# Revit family: Lighting-SIMES-S.5570W-MEGAZIP_DOWNLIGHT_ROUND
name_source: partatom
category: Lighting Fixtures
revit_build: Autodesk Revit 2016 (Build: 20150701_1515(x64)
units: mm (PartAtom-declared; Revit-internal decimal feet)

## family parameters
Cut with Voids When Loaded = No
Host = Face
Light Source = Yes
OmniClass Number = 23.80.70.14
OmniClass Title = Luminaries for External Lighting
Part Type = Normal
Room Calculation Point = No
Round Connector Dimension = Use Diameter
Shared = No

## types (1)
- Lighting-SIMES-S.5570W-MEGAZIP_DOWNLIGHT_ROUND
    Approval mark = CE
    BIMobject category = Outside
    Brand url = http://www.simes.it
    Color Filter = 16777215
    Color Rendering Index = CRI 90
    Colour Temperature = 3000
    Control Gear = magnetic transformer
    Date of publishing = 11/5/2015
    Default Elevation = 1219 mm
    Description = MEGAZIP DOWNLIGHT ROUND
Art. S.5570W.19
MODULES LED 3000K  230V 24.3W CRI 90
Rated luminaire luminous flux: 1280lm
Rated input power: 27W
Luminaire efficacy: 47lm/W
Electronic ballast 220÷240V 0/50/60Hz
CE

Fixture available with integral DALI driver on request with surcharge.

PRODUCT TYPE
False ceiling-recessed down-light fitting. Recessing depth 216 mm. IP rating IP 65
MATERIAL CHARACTERISTICS
"Copper Free" Aluminium die cast housing in EN AB-44100 with high resistance against corrosion. Stone wash surface treatment prior to painting process. 2 mm thick front trim in  Stainless Steel - Grade AISI 316L with 2,5-3% molybdenum content. A4 grade Stainless Steel screws with 2,5-3% molybdenum content which increases the resistance against corrosion. Pre treated Silicone Gaskets. Painting Process : 3 Step Process
1) Surface treatment with BONDERITE. A heavy metal free chemical surface treatment containing ceramic nano particles giving a cohesive, inorganic and highly dense protective coating. 2) PRE POLYMERIZATION a process of introducing an epoxy primer with excellent characteristics to the paint which also offers very high resistance to oxidation due to its Zinc content. 3) POLYMERIZATION a process with the application of polyester powder with high resistance against UV rays and harsh weather conditions. Resistance test protection for Marine applications for 1500h.  Mechanical resistance of diffuser IK 09
LIGHTING PERFORMANCE
Reflector in 99.98% pure anodized aluminium . Toughened  semiacid-etched  glass 12mm thick. Lamp  adjustable ±15° position. LOR -- 
INSTALLATION AND MANTEINANCE
The luminaires are fixed to the falseceiling by a heavy-duty bracket system, adjustable from inside the luminaire. Model comes with a steel safety wire. Front re-lamping without removing the complete fitting from the ceiling.
WIRING
Double cable entry with cable glands PG 13.5 (Ø 6÷12 mm) . Isolation: CLASS I . Available colours: Stainless steel (cod.19). Weight: 4.9 Kg Glow Wire test: 850°C
L.E.D circuit included.
This luminaire contains built-in LED modules with energy class: A, A+, A++. The LED modules cannot be changed in the luminaire (Regulation UE 874/2012).
LED circuit boards are engineered accordingly to actual Lumen Maintenance regulation (LM80) and Technical Memorandum (TM21) where uniformity and quality of light is 50.000 hours referred to L70  B20 Ta 25°C.Lifecycle refers to LED circuit boards only, all others components of the luminaire are excluded.

EMERGENCY VERSIONS The fittings operates both on AC ( 50/60Hz ) and DC ( 0Hz ) voltage.
    Design country = Italy
    Dimming Lamp Color Temperature Shift = <None>
    Edition number = 3
    Frequency = 0/50/60Hz
    IFC Classification = Light Fixture
    IK Rating = IK 09
    Installation instructions = http://www.simes.it
    Lamp = 1 LED
    Lamp Light Flux = 2124
    Lamp Power = 24,299999237060547
    Lamp count = 1
    Last Update = 28/11/2016 11:20:48
    Lifetime = 50000 L70 B20 Ta 25°C
    Light Output Ratio = 100
    Luminous efficacy = 47,399999999999999
    Manufacturer = SIMES
    Manufacturer country = Italy
    Manufacturer name = Simes
    Masterformat 2014 Code = 26 56 00
    Masterformat 2014 Description = Exterior Lighting
    Material main = Stainless steel
    Material secondary = Glass
    Model = S.5570W
    Mounting Place = Ceiling
    Mounting Type = Recessed
    Nominal height = 0
    Nominal width = 0
    OmniClass Code = 23-35 47 11
    OmniClass Description = Lighting Fixtures
    Photometric Web File = S5570W.ies
    Product Guid = c139a77d-b2a9-4fba-8ec3-c3d5a1cc7d48
    Product SKU = ZIP_DOWNLIGHT
    Product certification = http://www.simes.it
    Product data url = https://bimobject.com
    Product family = Downlight
    Product group = ZIP DOWNLIGHT
    Product url = http://www.simes.it
    Protection Class = Protection class I
    Protection Degree = IP 65
    QR code = http://bimobject.com
    System Light Flux = 1280
    System Power = 27
    Technical description = http://www.simes.it
    Tilt Angle = -90.00°
    Type Comments = SIMES S.p.A. - All rights reserved
    Type Image = megazipdown_tonda_semiacidato_led.jpg (2)
    UNSPSC Code = 3911
    URL = http://www.simes.it
    Uniclass 2015 Code = EF_70_80
    Uniclass 2015 Name = Lighting
    Voltage = 220÷240V
    Wattage Comments = 27.0W
    Weight Net (Kg) = 0

## geometry (parser evidence)
native form markers: Blend x2
no freeform markers — native parametric forms only
